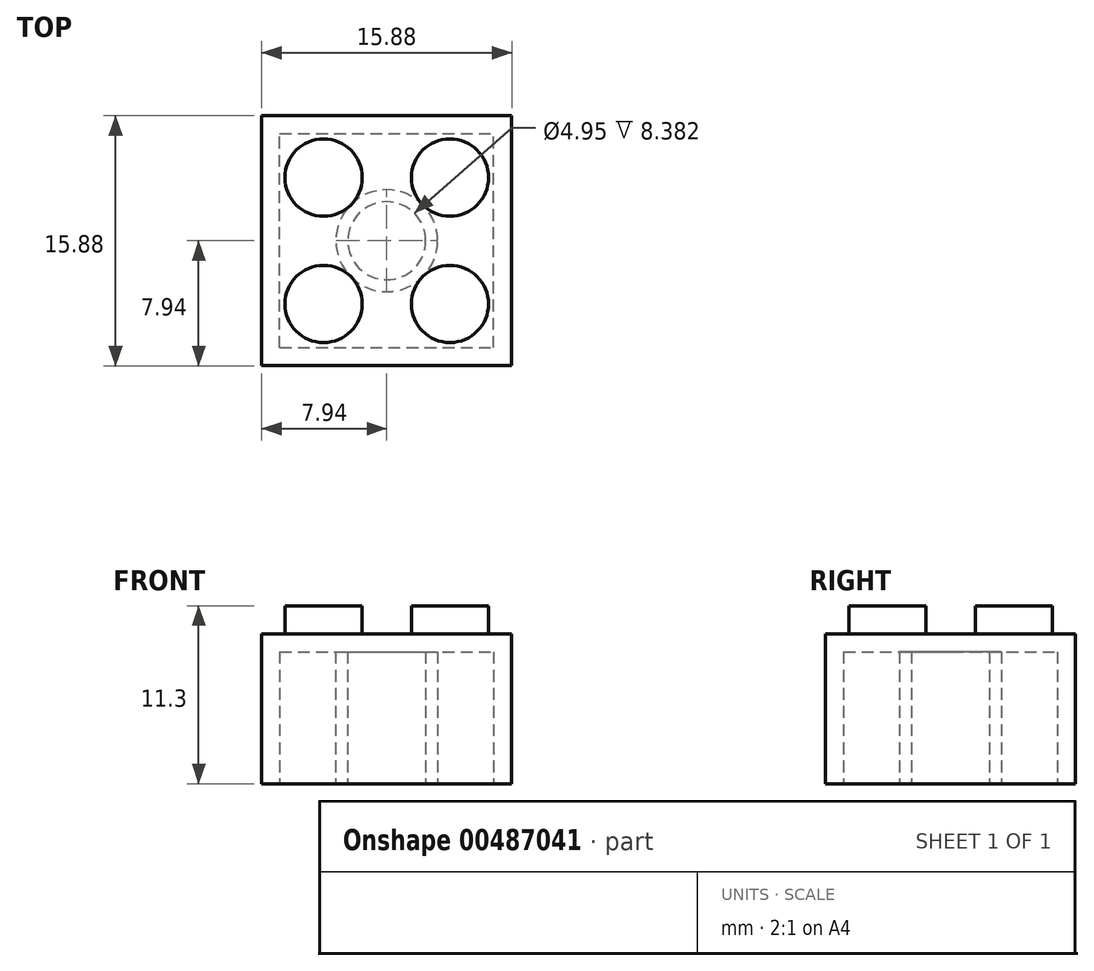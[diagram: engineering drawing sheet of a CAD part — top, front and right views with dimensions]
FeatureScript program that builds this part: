
annotation { "Feature Type Name" : "Feature", "Feature Type Description" : "" }
export const myFeature = defineFeature(function(context is Context, id is Id, definition is map)
    precondition{}
    {
        {
            var Q0;
            Q0=qCreatedBy(makeId("Top.planeOp"),FACE);
            var sketch = newSketch(context, id + "F0", { "sketchPlane" : qUnion([Q0])});
            skLineSegment(sketch, "E0.bottom", {"start": v(7.94, 7.94) * mm, "end": v(-7.94, 7.94) * mm});
            skLineSegment(sketch, "E0.top", {"start": v(7.94, -7.94) * mm, "end": v(-7.94, -7.94) * mm});
            skLineSegment(sketch, "E0.left", {"start": v(7.94, 7.94) * mm, "end": v(7.94, -7.94) * mm});
            skLineSegment(sketch, "E0.right", {"start": v(-7.94, 7.94) * mm, "end": v(-7.94, -7.94) * mm});
            skPoint(sketch, "E0.middle", {"position": v(0, 0) * mm});
            skSolve(sketch);
        }
        {
            var Q0;
            Q0=makeQuery(id+"F0.imprint","IMPRINT",FACE,{"disambiguationData":[TD([[makeQuery(id+"F0.imprint","IMPRINT",EDGE,{"derivedFrom":sQuery(id+"F0.wireOp",EDGE,"E0.bottom")}),1.0]])]});
            extrude(context, id + "F1", {"entities" : qUnion([Q0]), "endBound" : BoundingType.SYMMETRIC, "depth" : 9.52 * mm});
        }
        {
            var Q0;
            Q0=makeQuery(id+"F1.opExtrude","CAP_FACE",FACE,{"disambiguationData":[OSD([sQuery(id+"F0.wireOp",EDGE,"E0.bottom"),sQuery(id+"F0.wireOp",EDGE,"E0.top"),sQuery(id+"F0.wireOp",EDGE,"E0.left"),sQuery(id+"F0.wireOp",EDGE,"E0.right")])],"isStart":false});
            var sketch = newSketch(context, id + "F2", { "sketchPlane" : qUnion([Q0])});
            skCircle(sketch, "E1", {"center": v(-4.01, 4.01) * mm, "radius": 2.45 * mm});
            skCircle(sketch, "E2", {"center": v(4.01, 4.01) * mm, "radius": 2.45 * mm});
            skCircle(sketch, "E3", {"center": v(4.01, -4.01) * mm, "radius": 2.45 * mm});
            skCircle(sketch, "E4", {"center": v(-4.01, -4.01) * mm, "radius": 2.45 * mm});
            skSolve(sketch);
        }
        {
            var Q0;
            Q0=makeQuery(id+"F2.imprint","IMPRINT",FACE,{"disambiguationData":[TD([[makeQuery(id+"F2.imprint","IMPRINT",EDGE,{"derivedFrom":sQuery(id+"F2.wireOp",EDGE,"E4")}),1.0]])]});
            var Q1;
            Q1=makeQuery(id+"F2.imprint","IMPRINT",FACE,{"disambiguationData":[TD([[makeQuery(id+"F2.imprint","IMPRINT",EDGE,{"derivedFrom":sQuery(id+"F2.wireOp",EDGE,"E3")}),1.0]])]});
            var Q2;
            Q2=makeQuery(id+"F2.imprint","IMPRINT",FACE,{"disambiguationData":[TD([[makeQuery(id+"F2.imprint","IMPRINT",EDGE,{"derivedFrom":sQuery(id+"F2.wireOp",EDGE,"E2")}),1.0]])]});
            var Q3;
            Q3=makeQuery(id+"F2.imprint","IMPRINT",FACE,{"disambiguationData":[TD([[makeQuery(id+"F2.imprint","IMPRINT",EDGE,{"derivedFrom":sQuery(id+"F2.wireOp",EDGE,"E1")}),1.0]])]});
            extrude(context, id + "F3", {"entities" : qUnion([Q0, Q1, Q2, Q3]), "operationType" : NewBodyOperationType.ADD, "depth" : 1.78 * mm});
        }
        {
            var Q0;
            Q0=makeQuery(id+"F1.opExtrude","CAP_FACE",FACE,{"disambiguationData":[OSD([sQuery(id+"F0.wireOp",EDGE,"E0.bottom"),sQuery(id+"F0.wireOp",EDGE,"E0.top"),sQuery(id+"F0.wireOp",EDGE,"E0.left"),sQuery(id+"F0.wireOp",EDGE,"E0.right")])],"isStart":true});
            var sketch = newSketch(context, id + "F4", { "sketchPlane" : qUnion([Q0])});
            skLineSegment(sketch, "E5.bottom", {"start": v(-6.8, 6.8) * mm, "end": v(6.8, 6.8) * mm});
            skLineSegment(sketch, "E5.top", {"start": v(-6.8, -6.8) * mm, "end": v(6.8, -6.8) * mm});
            skLineSegment(sketch, "E5.left", {"start": v(-6.8, 6.8) * mm, "end": v(-6.8, -6.8) * mm});
            skLineSegment(sketch, "E5.right", {"start": v(6.8, 6.8) * mm, "end": v(6.8, -6.8) * mm});
            skPoint(sketch, "E5.middle", {"position": v(0, 0) * mm});
            skCircle(sketch, "E6", {"center": v(0, 0) * mm, "radius": 3.24 * mm});
            skCircle(sketch, "E7", {"center": v(0, 0) * mm, "radius": 2.48 * mm});
            skSolve(sketch);
        }
        {
            var Q0;
            Q0=makeQuery(id+"F4.imprint","IMPRINT",FACE,{"disambiguationData":[TD([[makeQuery(id+"F4.imprint","IMPRINT",EDGE,{"derivedFrom":sQuery(id+"F4.wireOp",EDGE,"E5.bottom")}),-1.0]])]});
            extrude(context, id + "F5", {"entities" : qUnion([Q0]), "operationType" : NewBodyOperationType.REMOVE, "oppositeDirection" : true, "depth" : 8.38 * mm});
        }
        {
            var Q0;
            Q0=makeQuery(id+"F5.boolean.opBoolean","SPLIT",FACE,{"disambiguationData":[TD([makeQuery(id+"F5.opExtrude","SWEPT_FACE",FACE,{"disambiguationData":[OSD([sQuery(id+"F4.wireOp",EDGE,"E6")])]})])],"derivedFrom":makeQuery(id+"F1.opExtrude","CAP_FACE",FACE,{"disambiguationData":[OSD([sQuery(id+"F0.wireOp",EDGE,"E0.bottom"),sQuery(id+"F0.wireOp",EDGE,"E0.top"),sQuery(id+"F0.wireOp",EDGE,"E0.left"),sQuery(id+"F0.wireOp",EDGE,"E0.right")])],"isStart":true})});
            var sketch = newSketch(context, id + "F6", { "sketchPlane" : qUnion([Q0])});
            skCircle(sketch, "E8", {"center": v(0, 0) * mm, "radius": 2.48 * mm});
            skSolve(sketch);
        }
        {
            var Q0;
            Q0=makeQuery(id+"F6.imprint","IMPRINT",FACE,{"disambiguationData":[TD([[makeQuery(id+"F6.imprint","IMPRINT",EDGE,{"derivedFrom":sQuery(id+"F6.wireOp",EDGE,"E8")}),1.0]])]});
            extrude(context, id + "F7", {"entities" : qUnion([Q0]), "operationType" : NewBodyOperationType.REMOVE, "oppositeDirection" : true, "depth" : 8.38 * mm});
        }
    });
